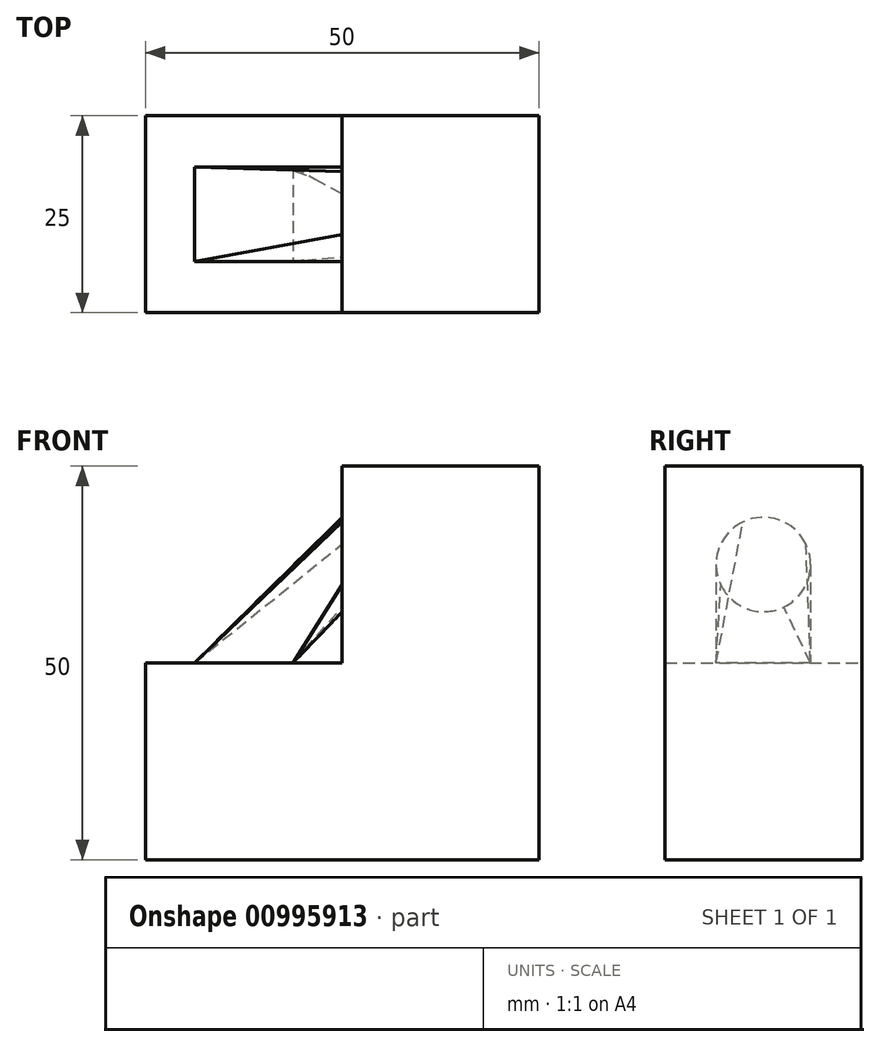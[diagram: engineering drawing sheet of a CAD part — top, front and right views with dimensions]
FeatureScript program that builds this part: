
annotation { "Feature Type Name" : "Feature", "Feature Type Description" : "" }
export const myFeature = defineFeature(function(context is Context, id is Id, definition is map)
    precondition{}
    {
        {
            var Q0;
            Q0=qCreatedBy(makeId("Front.planeOp"),FACE);
            var sketch = newSketch(context, id + "F0", { "sketchPlane" : qUnion([Q0])});
            skLineSegment(sketch, "E0", {"start": v(0, 0) * mm, "end": v(50, 0) * mm});
            skLineSegment(sketch, "E1", {"start": v(50, 0) * mm, "end": v(50, 50) * mm});
            skLineSegment(sketch, "E2", {"start": v(50, 50) * mm, "end": v(25, 50) * mm});
            skLineSegment(sketch, "E3", {"start": v(25, 50) * mm, "end": v(25, 25) * mm});
            skLineSegment(sketch, "E4", {"start": v(25, 25) * mm, "end": v(0, 25) * mm});
            skLineSegment(sketch, "E5", {"start": v(0, 25) * mm, "end": v(0, 0) * mm});
            skSolve(sketch);
        }
        {
            var Q0;
            Q0 = qSketchRegion(id + "F0", true);
            extrude(context, id + "F1", {"entities" : qUnion([Q0]), "depth" : 25 * mm, "offsetDistance" : 25 * mm});
        }
        {
            var Q0;
            Q0=makeQuery(id+"F1.opExtrude","SWEPT_FACE",FACE,{"disambiguationData":[OSD([sQuery(id+"F0.wireOp",EDGE,"E3")])]});
            var sketch = newSketch(context, id + "F2", { "sketchPlane" : qUnion([Q0])});
            skCircle(sketch, "E6", {"center": v(12.5, 37.5) * mm, "radius": 6 * mm});
            skSolve(sketch);
        }
        {
            var Q0;
            Q0=makeQuery(id+"F1.opExtrude","SWEPT_FACE",FACE,{"disambiguationData":[OSD([sQuery(id+"F0.wireOp",EDGE,"E4")])]});
            var sketch = newSketch(context, id + "F3", { "sketchPlane" : qUnion([Q0])});
            skLineSegment(sketch, "E7.bottom", {"start": v(18.75, -6.5) * mm, "end": v(6.25, -6.5) * mm});
            skLineSegment(sketch, "E7.top", {"start": v(18.75, -18.5) * mm, "end": v(6.25, -18.5) * mm});
            skLineSegment(sketch, "E7.left", {"start": v(18.75, -6.5) * mm, "end": v(18.75, -18.5) * mm});
            skLineSegment(sketch, "E7.right", {"start": v(6.25, -6.5) * mm, "end": v(6.25, -18.5) * mm});
            skPoint(sketch, "E7.middle", {"position": v(12.5, -12.5) * mm});
            skPoint(sketch, "E7.middle.positionSnap0", {"position": v(12.5, 0) * mm});
            skPoint(sketch, "E7.middle.positionSnap1", {"position": v(0, -12.5) * mm});
            skPoint(sketch, "E7.centerSnap0", {"position": v(12.5, 0) * mm});
            skPoint(sketch, "E7.centerSnap1", {"position": v(0, -12.5) * mm});
            skSolve(sketch);
        }
        {
            var Q1;
            Q1 = qSketchRegion(id + "F3", true);
            var Q2;
            Q2 = qSketchRegion(id + "F2", true);
            loft(context, id + "F4", {"operationType" : NewBodyOperationType.ADD, "sheetProfilesArray" : [{ "sheetProfileEntities" : qUnion([Q1]) }, { "sheetProfileEntities" : qUnion([Q2]) }]});
        }
    });
